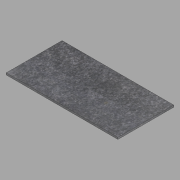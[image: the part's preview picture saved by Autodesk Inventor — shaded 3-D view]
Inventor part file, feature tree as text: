
AUTODESK INVENTOR PART (.ipt)
format: ipt  version: 2022.2 (Build 262287000, 287)  size: 109,568 bytes
history: native  units: in
note: dims shown in document units (in); Inventor stores cm internally (conversion verified against a paired STEP export)
features: extrude x1, sketch x1
ambient origin geometry x8: Origin, YZ Plane, XZ Plane, XY Plane, X Axis, Y Axis, Z Axis, Center Point
bodies: Solid1 (feature_tree)
feature tree (2):
  extrude  "Extrusion1"  Depth=30.0in
  sketch  "Sketch1"  dims[d0=60.0in d1=30.0in d2=1.0in d3=0.0in]
